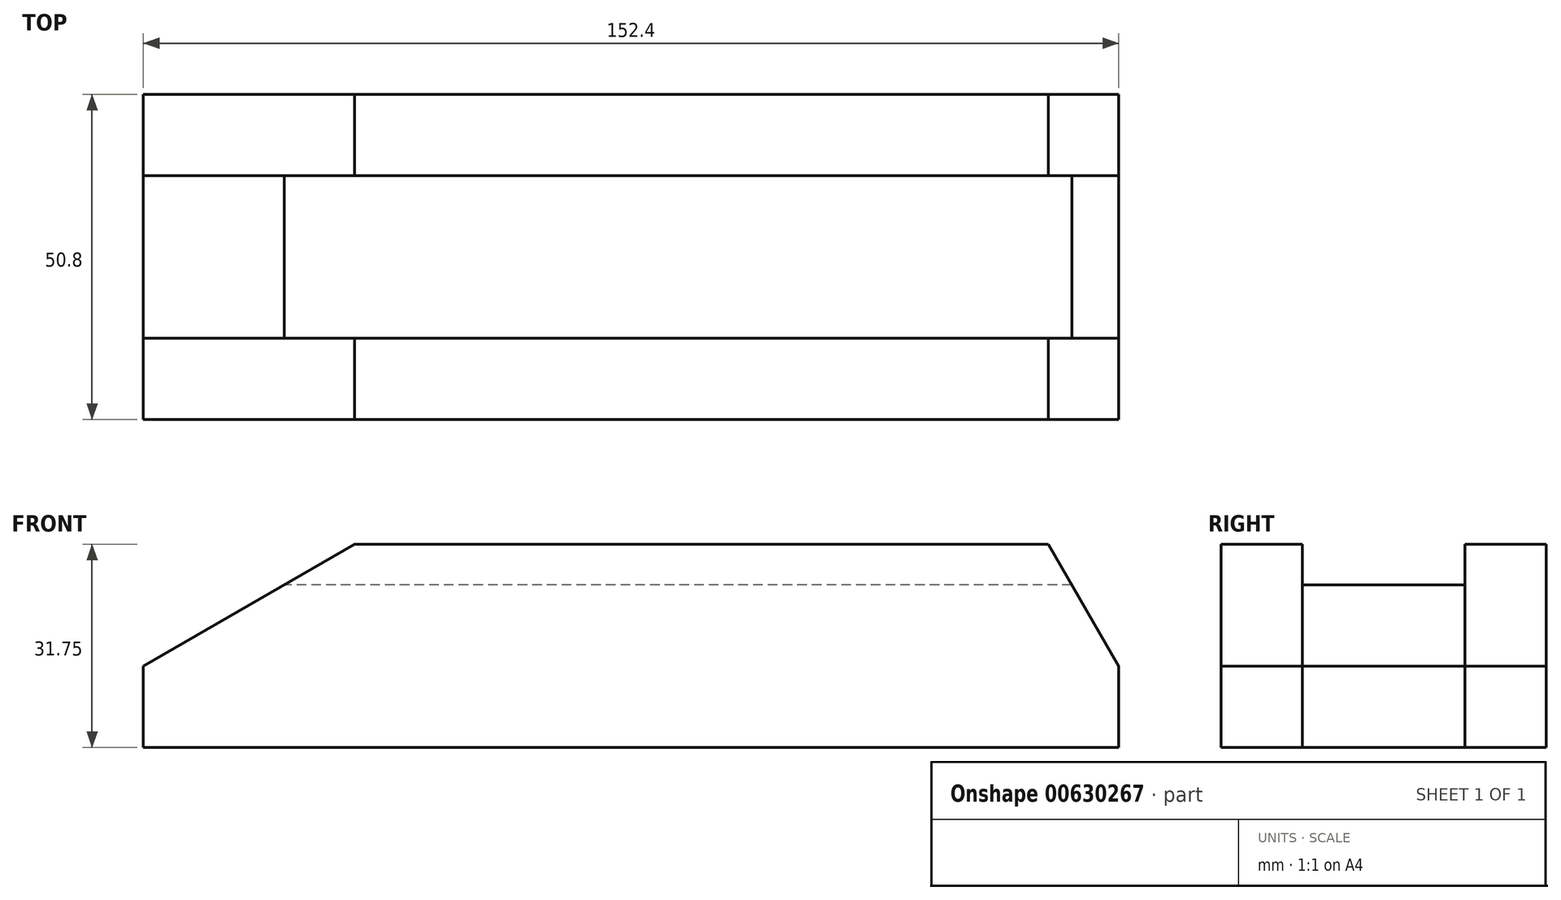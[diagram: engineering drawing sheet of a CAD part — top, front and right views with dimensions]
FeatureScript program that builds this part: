
annotation { "Feature Type Name" : "Feature", "Feature Type Description" : "" }
export const myFeature = defineFeature(function(context is Context, id is Id, definition is map)
    precondition{}
    {
        {
            var Q0;
            Q0=qCreatedBy(makeId("Right.planeOp"),FACE);
            var sketch = newSketch(context, id + "F0", { "sketchPlane" : qUnion([Q0])});
            skLineSegment(sketch, "E0.bottom", {"start": v(0, 0) * mm, "end": v(12.7, 0) * mm});
            skLineSegment(sketch, "E0.top", {"start": v(0, 31.75) * mm, "end": v(12.7, 31.75) * mm});
            skLineSegment(sketch, "E0.left", {"start": v(0, 0) * mm, "end": v(0, 31.75) * mm});
            skLineSegment(sketch, "E0.right", {"start": v(12.7, 0) * mm, "end": v(12.7, 31.75) * mm});
            skLineSegment(sketch, "E1.bottom", {"start": v(12.7, 0) * mm, "end": v(38.1, 0) * mm});
            skLineSegment(sketch, "E1.top", {"start": v(12.7, 25.4) * mm, "end": v(38.1, 25.4) * mm});
            skLineSegment(sketch, "E1.left", {"start": v(12.7, 0) * mm, "end": v(12.7, 25.4) * mm});
            skLineSegment(sketch, "E1.right", {"start": v(38.1, 0) * mm, "end": v(38.1, 25.4) * mm});
            skLineSegment(sketch, "E2.bottom", {"start": v(38.1, 0) * mm, "end": v(50.8, 0) * mm});
            skLineSegment(sketch, "E2.top", {"start": v(38.1, 31.75) * mm, "end": v(50.8, 31.75) * mm});
            skLineSegment(sketch, "E2.left", {"start": v(38.1, 0) * mm, "end": v(38.1, 31.75) * mm});
            skLineSegment(sketch, "E2.right", {"start": v(50.8, 0) * mm, "end": v(50.8, 31.75) * mm});
            skSolve(sketch);
        }
        {
            var Q0;
            Q0=makeQuery(id+"F0.imprint","IMPRINT",FACE,{"disambiguationData":[TD([[makeQuery(id+"F0.imprint","IMPRINT",EDGE,{"derivedFrom":sQuery(id+"F0.wireOp",EDGE,"E0.bottom")}),1.0]])]});
            var Q1;
            {var subQ3=sQuery(id+"F0.wireOp",EDGE,"E2.bottom");Q1=makeQuery(id+"F0.imprint","IMPRINT",FACE,{"disambiguationData":[TD([[makeQuery(id+"F0.imprint","IMPRINT",EDGE,{"derivedFrom":subQ3}),1.0]])]});}
            extrude(context, id + "F1", {"entities" : qUnion([Q0, Q1]), "depth" : 152.4 * mm, "offsetDistance" : 25.4 * mm});
        }
        {
            var Q0;
            {var subQ0=sQuery(id+"F0.wireOp",EDGE,"E1.bottom");Q0=makeQuery(id+"F0.imprint","IMPRINT",FACE,{"disambiguationData":[TD([[makeQuery(id+"F0.imprint","IMPRINT",EDGE,{"derivedFrom":subQ0}),1.0]])]});}
            var Q1;
            Q1=makeQuery(id+"F1.opExtrude","CAP_FACE",FACE,{"disambiguationData":[OSD([sQuery(id+"F0.wireOp",EDGE,"E0.bottom"),sQuery(id+"F0.wireOp",EDGE,"E0.top"),sQuery(id+"F0.wireOp",EDGE,"E0.left"),sQuery(id+"F0.wireOp",EDGE,"E0.right"),sQuery(id+"F0.wireOp",EDGE,"E1.left")])],"isStart":false});
            extrude(context, id + "F2", {"entities" : qUnion([Q0]), "endBound" : BoundingType.UP_TO_SURFACE, "depth" : 25.4 * mm, "endBoundEntityFace" : qUnion([Q1]), "offsetDistance" : 25.4 * mm});
        }
        {
            var Q0;
            Q0=makeQuery(id+"F1.opExtrude","SWEPT_FACE",FACE,{"disambiguationData":[OSD([sQuery(id+"F0.wireOp",EDGE,"E0.left")])]});
            var sketch = newSketch(context, id + "F3", { "sketchPlane" : qUnion([Q0])});
            skLineSegment(sketch, "E3", {"start": v(152.4, 12.7) * mm, "end": v(141.4, 31.75) * mm});
            skLineSegment(sketch, "E4", {"start": v(141.4, 31.75) * mm, "end": v(152.4, 31.75) * mm});
            skLineSegment(sketch, "E5", {"start": v(152.4, 31.75) * mm, "end": v(152.4, 12.7) * mm});
            skLineSegment(sketch, "E6", {"start": v(0, 12.7) * mm, "end": v(33, 31.75) * mm});
            skLineSegment(sketch, "E7", {"start": v(33, 31.75) * mm, "end": v(0, 31.75) * mm});
            skLineSegment(sketch, "E8", {"start": v(0, 31.75) * mm, "end": v(0, 12.7) * mm});
            skSolve(sketch);
        }
        {
            var Q0;
            Q0=qSketchRegion(id+"F3",true);
            extrude(context, id + "F4", {"entities" : qUnion([Q0]), "operationType" : NewBodyOperationType.REMOVE, "endBound" : BoundingType.THROUGH_ALL, "oppositeDirection" : true, "depth" : 25.4 * mm, "offsetDistance" : 25.4 * mm});
        }
    });
